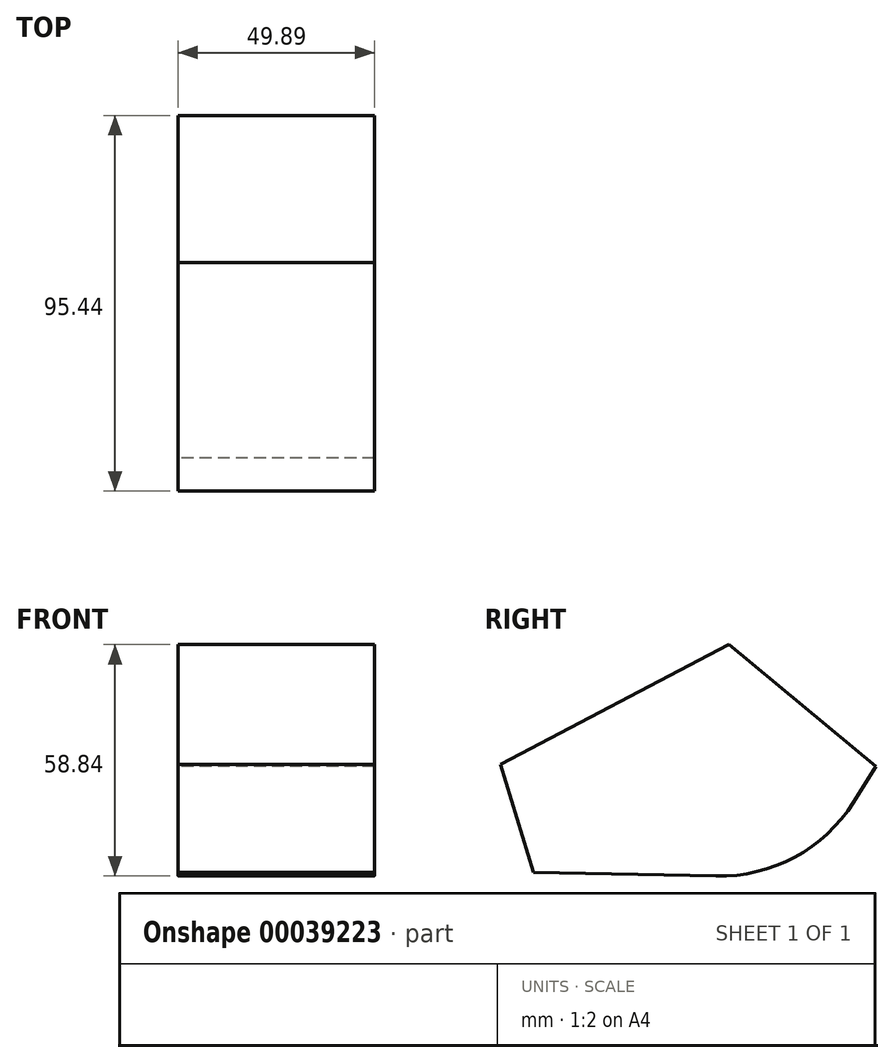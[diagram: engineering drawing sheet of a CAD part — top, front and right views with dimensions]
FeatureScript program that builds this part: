
annotation { "Feature Type Name" : "Feature", "Feature Type Description" : "" }
export const myFeature = defineFeature(function(context is Context, id is Id, definition is map)
    precondition{}
    {
        {
            var Q0;
            Q0=qCreatedBy(makeId("Right.planeOp"),FACE);
            var sketch = newSketch(context, id + "F0", { "sketchPlane" : qUnion([Q0])});
            skLineSegment(sketch, "E0", {"start": v(-24.45, 3.66) * mm, "end": v(33.58, 34.13) * mm});
            skLineSegment(sketch, "E1", {"start": v(33.58, 34.13) * mm, "end": v(70.99, 3.1) * mm});
            skLineSegment(sketch, "E2", {"start": v(70.99, 3.1) * mm, "end": v(53.1, -25.18) * mm});
            skLineSegment(sketch, "E3", {"start": v(53.1, -25.18) * mm, "end": v(-16.06, -23.72) * mm});
            skLineSegment(sketch, "E4", {"start": v(-16.06, -23.72) * mm, "end": v(-24.45, 3.66) * mm});
            skSolve(sketch);
        }
        {
            var Q0;
            Q0=makeQuery(id+"F0.imprint","IMPRINT",FACE,{"disambiguationData":[TD([[makeQuery(id+"F0.imprint","IMPRINT",EDGE,{"derivedFrom":sQuery(id+"F0.wireOp",EDGE,"E0")}),-1.0]])]});
            extrude(context, id + "F1", {"entities" : qUnion([Q0]), "depth" : 49.9 * mm});
        }
        {
            var Q0;
            Q0=makeQuery(id+"F1.opExtrude","SWEPT_EDGE",EDGE,{"disambiguationData":[OSD([sQuery(id+"F0.wireOp",EDGE,"E2"),sQuery(id+"F0.wireOp",EDGE,"E3")])]});
            fillet(context, id + "F2", {"entities" : qUnion([Q0]), "radius" : 40.3 * mm, "tangentPropagation" : true, "allowEdgeOverflow" : false});
        }
    });
